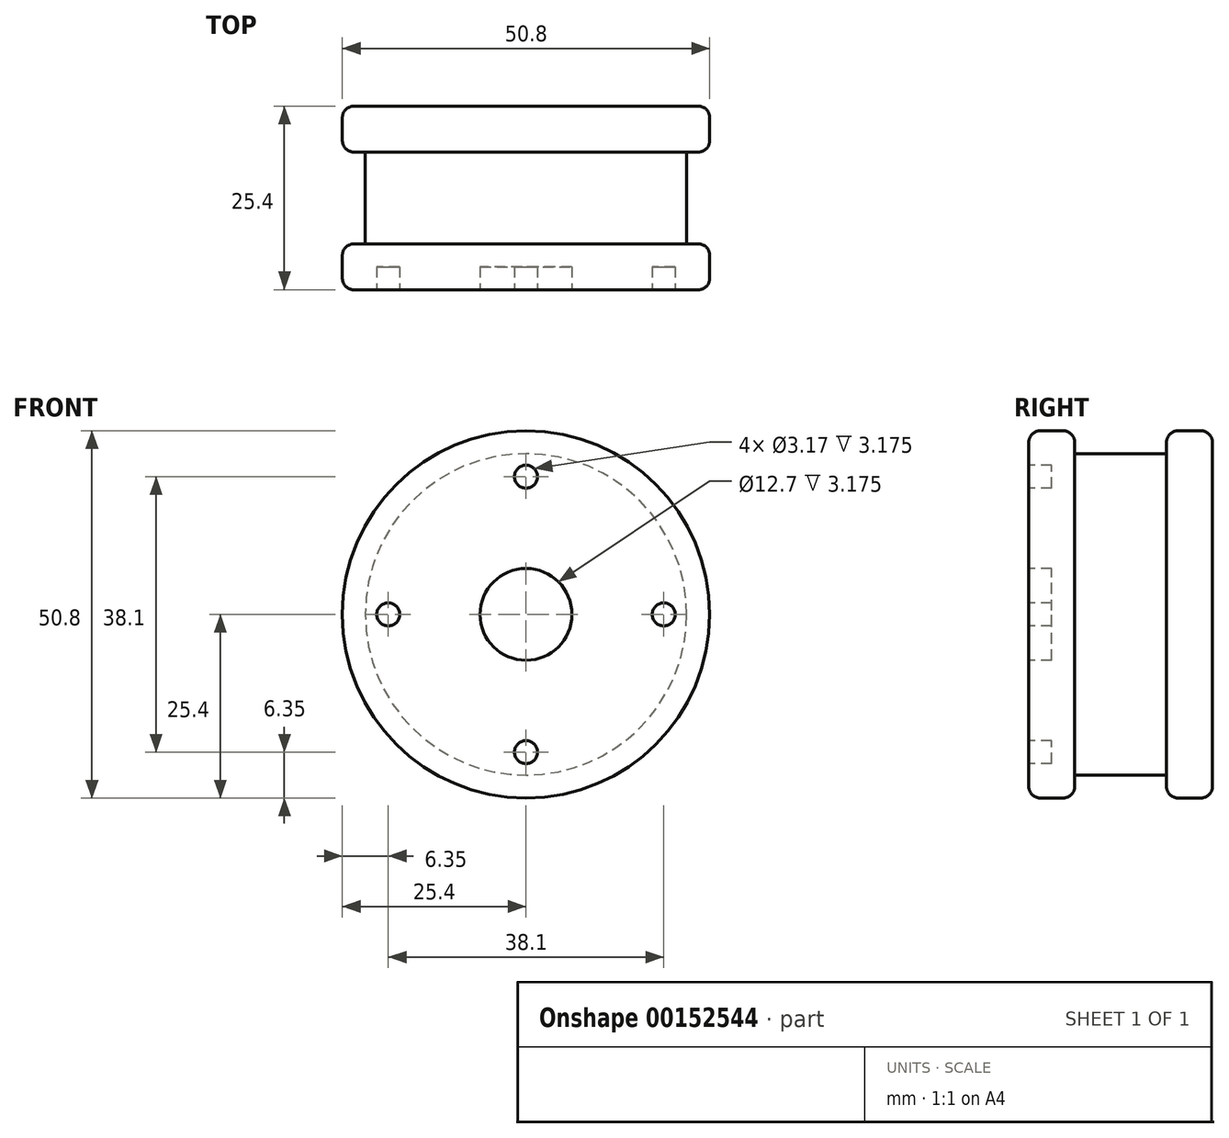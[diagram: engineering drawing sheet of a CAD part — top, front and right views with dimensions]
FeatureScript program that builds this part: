
annotation { "Feature Type Name" : "Feature", "Feature Type Description" : "" }
export const myFeature = defineFeature(function(context is Context, id is Id, definition is map)
    precondition{}
    {
        {
            var Q0;
            Q0=qCreatedBy(makeId("Front.planeOp"),FACE);
            var sketch = newSketch(context, id + "F0", { "sketchPlane" : qUnion([Q0])});
            skCircle(sketch, "E0", {"center": v(0, 0) * mm, "radius": 25.4 * mm});
            skSolve(sketch);
        }
        {
            var Q0;
            Q0 = qSketchRegion(id + "F0", true);
            extrude(context, id + "F1", {"entities" : qUnion([Q0]), "depth" : 6.35 * mm});
        }
        {
            var Q0;
            Q0=makeQuery(id+"F1.opExtrude","CAP_FACE",FACE,{"disambiguationData":[OSD([sQuery(id+"F0.wireOp",EDGE,"E0")])],"isStart":false});
            var sketch = newSketch(context, id + "F2", { "sketchPlane" : qUnion([Q0])});
            skCircle(sketch, "E1", {"center": v(0, 0) * mm, "radius": 22.23 * mm});
            skSolve(sketch);
        }
        {
            var Q0;
            Q0 = qSketchRegion(id + "F2", true);
            extrude(context, id + "F3", {"entities" : qUnion([Q0]), "operationType" : NewBodyOperationType.ADD, "depth" : 12.7 * mm});
        }
        {
            var Q0;
            Q0=makeQuery(id+"F3.opExtrude","CAP_FACE",FACE,{"disambiguationData":[OSD([sQuery(id+"F2.wireOp",EDGE,"E1")])],"isStart":false});
            var sketch = newSketch(context, id + "F4", { "sketchPlane" : qUnion([Q0])});
            skCircle(sketch, "E2", {"center": v(0, 0) * mm, "radius": 25.4 * mm});
            skSolve(sketch);
        }
        {
            var Q0;
            Q0 = qSketchRegion(id + "F4", true);
            extrude(context, id + "F5", {"entities" : qUnion([Q0]), "operationType" : NewBodyOperationType.ADD, "depth" : 6.35 * mm});
        }
        {
            var Q0;
            Q0=makeQuery(id+"F1.opExtrude","SWEPT_FACE",FACE,{"disambiguationData":[OSD([sQuery(id+"F0.wireOp",EDGE,"E0")])]});
            var Q1;
            Q1=makeQuery(id+"F5.opExtrude","SWEPT_FACE",FACE,{"disambiguationData":[OSD([sQuery(id+"F4.wireOp",EDGE,"E2")])]});
            fillet(context, id + "F6", {"entities" : qUnion([Q0, Q1]), "radius" : 1.6 * mm, "tangentPropagation" : true, "allowEdgeOverflow" : false});
        }
        {
            var Q0;
            Q0=makeQuery(id+"F5.opExtrude","CAP_FACE",FACE,{"disambiguationData":[OSD([sQuery(id+"F4.wireOp",EDGE,"E2")])],"isStart":false});
            var sketch = newSketch(context, id + "F7", { "sketchPlane" : qUnion([Q0])});
            skCircle(sketch, "E3", {"center": v(0, 0) * mm, "radius": 6.35 * mm});
            skCircle(sketch, "E4", {"center": v(0, 19.05) * mm, "radius": 1.59 * mm});
            skCircle(sketch, "E5", {"center": v(19.05, 0) * mm, "radius": 1.59 * mm});
            skCircle(sketch, "E6", {"center": v(0, -19.05) * mm, "radius": 1.59 * mm});
            skCircle(sketch, "E7", {"center": v(-19.05, 0) * mm, "radius": 1.59 * mm});
            skSolve(sketch);
        }
        {
            var Q0;
            Q0 = qSketchRegion(id + "F7", true);
            extrude(context, id + "F8", {"entities" : qUnion([Q0]), "operationType" : NewBodyOperationType.REMOVE, "oppositeDirection" : true, "depth" : 3.17 * mm});
        }
    });
